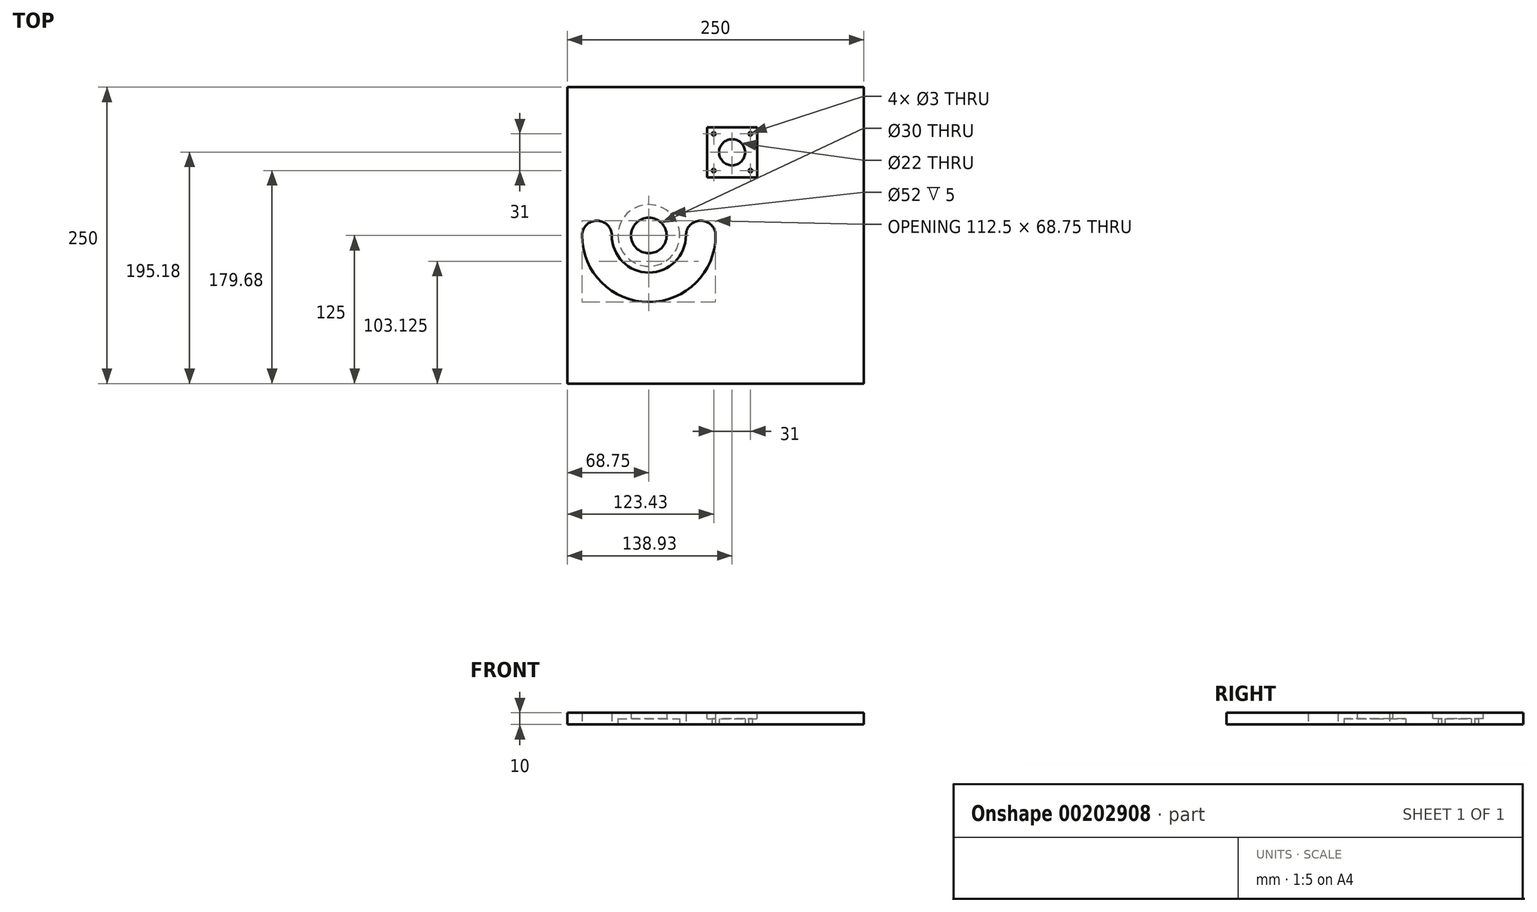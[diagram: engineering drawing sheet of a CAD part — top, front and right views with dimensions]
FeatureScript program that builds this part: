
annotation { "Feature Type Name" : "Feature", "Feature Type Description" : "" }
export const myFeature = defineFeature(function(context is Context, id is Id, definition is map)
    precondition{}
    {
        {
            var Q0;
            Q0=qCreatedBy(makeId("Top.planeOp"),FACE);
            var sketch = newSketch(context, id + "F0", { "sketchPlane" : qUnion([Q0])});
            skPoint(sketch, "E0.middle", {"position": v(0, -3.22) * mm});
            skArc(sketch, "E1", {"start": v(-112.5, 0) * mm, "mid": v(-56.25, -56.25) * mm, "end": v(0, 0) * mm});
            skArc(sketch, "E2", {"start": v(-87.5, 0) * mm, "mid": v(-56.25, -31.25) * mm, "end": v(-25, 0) * mm});
            skArc(sketch, "E3", {"start": v(0, 0) * mm, "mid": v(-12.5, 12.5) * mm, "end": v(-25, 0) * mm});
            skArc(sketch, "E4", {"start": v(-87.5, 0) * mm, "mid": v(-100, 12.5) * mm, "end": v(-112.5, 0) * mm});
            skLineSegment(sketch, "E5.bottom", {"start": v(-125, 125) * mm, "end": v(125, 125) * mm});
            skLineSegment(sketch, "E5.top", {"start": v(-125, -125) * mm, "end": v(125, -125) * mm});
            skLineSegment(sketch, "E5.left", {"start": v(-125, 125) * mm, "end": v(-125, -125) * mm});
            skLineSegment(sketch, "E5.right", {"start": v(125, 125) * mm, "end": v(125, -125) * mm});
            skPoint(sketch, "E5.middle", {"position": v(0, 0) * mm});
            skCircle(sketch, "E6", {"center": v(-56.25, 0) * mm, "radius": 15 * mm});
            skCircle(sketch, "E7", {"center": v(13.93, 70.18) * mm, "radius": 11 * mm});
            skCircle(sketch, "E8", {"center": v(29.43, 85.68) * mm, "radius": 1.5 * mm});
            skCircle(sketch, "E9", {"center": v(-1.57, 85.68) * mm, "radius": 1.5 * mm});
            skCircle(sketch, "E10", {"center": v(29.43, 54.68) * mm, "radius": 1.5 * mm});
            skCircle(sketch, "E11", {"center": v(-1.57, 54.68) * mm, "radius": 1.5 * mm});
            skSolve(sketch);
        }
        {
            var Q0;
            Q0=makeQuery(id+"F0.imprint","IMPRINT",FACE,{"disambiguationData":[TD([[makeQuery(id+"F0.imprint","IMPRINT",EDGE,{"derivedFrom":sQuery(id+"F0.wireOp",EDGE,"E1")}),-1.0]])]});
            extrude(context, id + "F1", {"entities" : qUnion([Q0]), "depth" : 10 * mm});
        }
        {
            var Q0;
            Q0=makeQuery(id+"F1.opExtrude","CAP_FACE",FACE,{"disambiguationData":[OSD([sQuery(id+"F0.wireOp",EDGE,"E1"),sQuery(id+"F0.wireOp",EDGE,"E2"),sQuery(id+"F0.wireOp",EDGE,"E3"),sQuery(id+"F0.wireOp",EDGE,"E4"),sQuery(id+"F0.wireOp",EDGE,"E5.bottom"),sQuery(id+"F0.wireOp",EDGE,"E5.top"),sQuery(id+"F0.wireOp",EDGE,"E5.left"),sQuery(id+"F0.wireOp",EDGE,"E5.right")])],"isStart":true});
            var sketch = newSketch(context, id + "F2", { "sketchPlane" : qUnion([Q0])});
            skLineSegment(sketch, "E12", {"start": v(-56.25, 31.25) * mm, "end": v(-56.25, 0) * mm});
            skCircle(sketch, "E13", {"center": v(-56.25, 0) * mm, "radius": 26 * mm});
            skCircle(sketch, "E14", {"center": v(-56.25, 0) * mm, "radius": 10 * mm});
            skSolve(sketch);
        }
        {
            var Q0;
            Q0=makeQuery(id+"F1.opExtrude","CAP_FACE",FACE,{"disambiguationData":[OSD([sQuery(id+"F0.wireOp",EDGE,"E1"),sQuery(id+"F0.wireOp",EDGE,"E2"),sQuery(id+"F0.wireOp",EDGE,"E3"),sQuery(id+"F0.wireOp",EDGE,"E4"),sQuery(id+"F0.wireOp",EDGE,"E5.bottom"),sQuery(id+"F0.wireOp",EDGE,"E5.top"),sQuery(id+"F0.wireOp",EDGE,"E5.left"),sQuery(id+"F0.wireOp",EDGE,"E5.right"),sQuery(id+"F0.wireOp",EDGE,"E6"),sQuery(id+"F0.wireOp",EDGE,"E7")])],"isStart":false});
            var sketch = newSketch(context, id + "F3", { "sketchPlane" : qUnion([Q0])});
            skLineSegment(sketch, "E15.bottom", {"start": v(-7.22, 91.33) * mm, "end": v(35.08, 91.33) * mm});
            skLineSegment(sketch, "E15.top", {"start": v(-7.22, 49.03) * mm, "end": v(35.08, 49.03) * mm});
            skLineSegment(sketch, "E15.left", {"start": v(-7.22, 91.33) * mm, "end": v(-7.22, 49.03) * mm});
            skLineSegment(sketch, "E15.right", {"start": v(35.08, 91.33) * mm, "end": v(35.08, 49.03) * mm});
            skPoint(sketch, "E15.middle", {"position": v(13.93, 70.18) * mm});
            skSolve(sketch);
        }
        {
            var Q0;
            Q0 = qSketchRegion(id + "F3", true);
            extrude(context, id + "F4", {"entities" : qUnion([Q0]), "operationType" : NewBodyOperationType.REMOVE, "oppositeDirection" : true, "depth" : 5 * mm});
        }
        {
            var Q0;
            Q0=makeQuery(id+"F2.imprint","IMPRINT",FACE,{"disambiguationData":[TD([[makeQuery(id+"F2.imprint","IMPRINT",EDGE,{"derivedFrom":sQuery(id+"F2.wireOp",EDGE,"E13")}),1.0]])]});
            extrude(context, id + "F5", {"entities" : qUnion([Q0]), "operationType" : NewBodyOperationType.REMOVE, "oppositeDirection" : true, "depth" : 5 * mm});
        }
        {
            var Q0;
            Q0=makeQuery(id+"F1.opExtrude","SWEPT_BODY",BODY,{"disambiguationData":[OSD([sQuery(id+"F0.wireOp",EDGE,"E1"),sQuery(id+"F0.wireOp",EDGE,"E2"),sQuery(id+"F0.wireOp",EDGE,"E3"),sQuery(id+"F0.wireOp",EDGE,"E4"),sQuery(id+"F0.wireOp",EDGE,"E5.bottom"),sQuery(id+"F0.wireOp",EDGE,"E5.top"),sQuery(id+"F0.wireOp",EDGE,"E5.left"),sQuery(id+"F0.wireOp",EDGE,"E5.right"),sQuery(id+"F0.wireOp",EDGE,"E6"),sQuery(id+"F0.wireOp",EDGE,"E7"),sQuery(id+"F0.wireOp",EDGE,"E8"),sQuery(id+"F0.wireOp",EDGE,"E9"),sQuery(id+"F0.wireOp",EDGE,"E10"),sQuery(id+"F0.wireOp",EDGE,"E11")])]});
            transform(context, id + "F6", {"entities" : qUnion([Q0]), "transformType" : TransformType.TRANSLATION_3D, "dx" : 0 * mm, "dy" : 0 * mm, "dz" : 0 * mm, "makeCopy" : true});
        }
        {
            var Q0;
            Q0=makeQuery(id+"F6.opPattern","COPY",BODY,{"derivedFrom":makeQuery(id+"F1.opExtrude","SWEPT_BODY",BODY,{"disambiguationData":[OSD([sQuery(id+"F0.wireOp",EDGE,"E1"),sQuery(id+"F0.wireOp",EDGE,"E2"),sQuery(id+"F0.wireOp",EDGE,"E3"),sQuery(id+"F0.wireOp",EDGE,"E4"),sQuery(id+"F0.wireOp",EDGE,"E5.bottom"),sQuery(id+"F0.wireOp",EDGE,"E5.top"),sQuery(id+"F0.wireOp",EDGE,"E5.left"),sQuery(id+"F0.wireOp",EDGE,"E5.right"),sQuery(id+"F0.wireOp",EDGE,"E6"),sQuery(id+"F0.wireOp",EDGE,"E7"),sQuery(id+"F0.wireOp",EDGE,"E8"),sQuery(id+"F0.wireOp",EDGE,"E9"),sQuery(id+"F0.wireOp",EDGE,"E10"),sQuery(id+"F0.wireOp",EDGE,"E11")])]}),"instanceName":"1"});
            deleteBodies(context, id + "F7", {"entities" : qUnion([Q0])});
        }
    });
